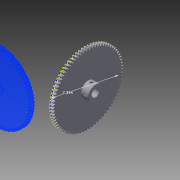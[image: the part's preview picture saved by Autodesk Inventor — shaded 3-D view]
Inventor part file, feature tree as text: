
AUTODESK INVENTOR PART (.ipt)
format: ipt  version: 2012 (Build 160160000, 160)  size: 1,860,096 bytes
history: native  units: in
note: dims shown in document units (in); Inventor stores cm internally (conversion verified against a paired STEP export)
features: imported_body x2, sketch x1
ambient origin geometry x8: Origin, YZ Plane, XZ Plane, XY Plane, X Axis, Y Axis, Z Axis, Center Point
feature tree (3):
  sketch  "Sketch1"  dims[d0=2.3438in]
  imported_body  "Base1"
  imported_body  "Base2"
